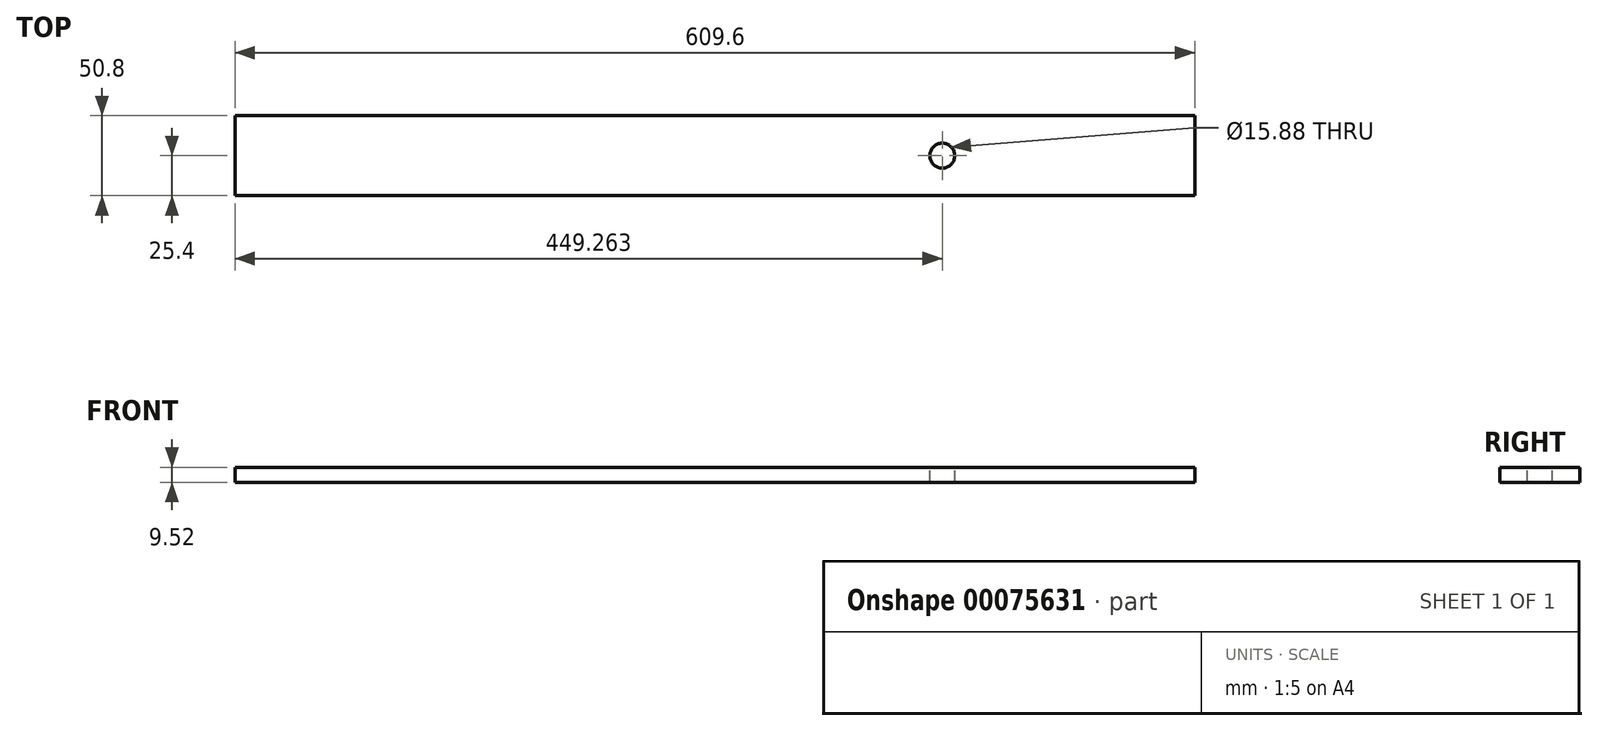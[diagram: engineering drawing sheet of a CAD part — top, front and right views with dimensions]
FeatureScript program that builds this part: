
annotation { "Feature Type Name" : "Feature", "Feature Type Description" : "" }
export const myFeature = defineFeature(function(context is Context, id is Id, definition is map)
    precondition{}
    {
        {
            var Q0;
            Q0=qCreatedBy(makeId("Right.planeOp"),FACE);
            var sketch = newSketch(context, id + "F0", { "sketchPlane" : qUnion([Q0])});
            skLineSegment(sketch, "E0.rect.bottom", {"start": v(25.4, 4.76) * mm, "end": v(-25.4, 4.76) * mm});
            skLineSegment(sketch, "E0.rect.top", {"start": v(25.4, -4.76) * mm, "end": v(-25.4, -4.76) * mm});
            skLineSegment(sketch, "E0.rect.left", {"start": v(25.4, 4.76) * mm, "end": v(25.4, -4.76) * mm});
            skLineSegment(sketch, "E0.rect.right", {"start": v(-25.4, 4.76) * mm, "end": v(-25.4, -4.76) * mm});
            skPoint(sketch, "E0.rect.middle", {"position": v(0, 0) * mm});
            skSolve(sketch);
        }
        {
            var Q0;
            Q0=makeQuery(id+"F0.imprint","IMPRINT",FACE,{"disambiguationData":[TD([[makeQuery(id+"F0.imprint","IMPRINT",EDGE,{"derivedFrom":sQuery(id+"F0.wireOp",EDGE,"E0.rect.bottom")}),1.0]])]});
            var Q1;
            Q1 = qSketchRegion(id + "F0", true);
            extrude(context, id + "F1", {"entities" : qUnion([Q0, Q1]), "endBound" : BoundingType.SYMMETRIC, "depth" : 609.6 * mm});
        }
        {
            var Q0;
            Q0=makeQuery(id+"F1.opExtrude","SWEPT_FACE",FACE,{"disambiguationData":[OSD([sQuery(id+"F0.wireOp",EDGE,"E0.rect.bottom")])]});
            var sketch = newSketch(context, id + "F2", { "sketchPlane" : qUnion([Q0])});
            skCircle(sketch, "E1", {"center": v(144.46, 0) * mm, "radius": 7.94 * mm});
            skSolve(sketch);
        }
        {
            var Q0;
            Q0 = qSketchRegion(id + "F2", true);
            extrude(context, id + "F3", {"entities" : qUnion([Q0]), "operationType" : NewBodyOperationType.REMOVE, "endBound" : BoundingType.THROUGH_ALL, "oppositeDirection" : true, "depth" : 25.4 * mm});
        }
    });
